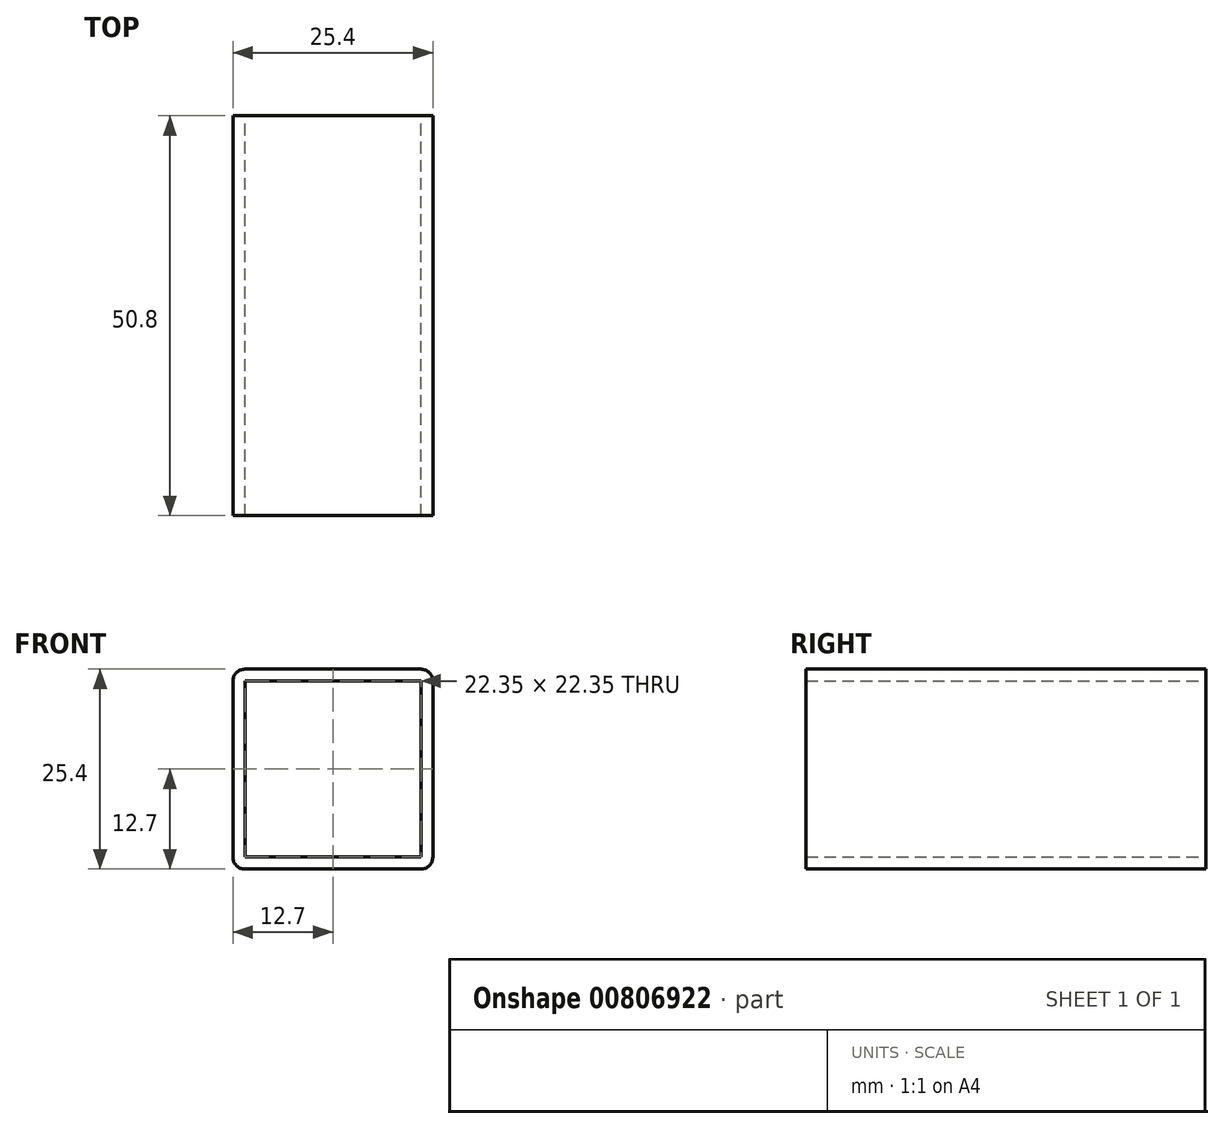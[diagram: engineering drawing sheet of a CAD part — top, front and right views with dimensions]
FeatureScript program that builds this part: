
annotation { "Feature Type Name" : "Feature", "Feature Type Description" : "" }
export const myFeature = defineFeature(function(context is Context, id is Id, definition is map)
    precondition{}
    {
        {
            var Q0;
            Q0=qCreatedBy(makeId("Front.planeOp"),FACE);
            var sketch = newSketch(context, id + "F0", { "sketchPlane" : qUnion([Q0])});
            skLineSegment(sketch, "E0.bottom", {"start": v(1.52, 0) * mm, "end": v(23.88, 0) * mm});
            skLineSegment(sketch, "E0.top", {"start": v(1.52, 25.4) * mm, "end": v(23.88, 25.4) * mm});
            skLineSegment(sketch, "E0.left", {"start": v(0, 1.52) * mm, "end": v(0, 23.88) * mm});
            skLineSegment(sketch, "E0.right", {"start": v(25.4, 1.52) * mm, "end": v(25.4, 23.88) * mm});
            skPoint(sketch, "E1.visualSharp", {"position": v(0, 25.4) * mm});
            skArc(sketch, "E1.filletArc", {"start": v(1.52, 25.4) * mm, "mid": v(0.45, 24.95) * mm, "end": v(0, 23.88) * mm});
            skPoint(sketch, "E2.visualSharp", {"position": v(25.4, 25.4) * mm});
            skArc(sketch, "E2.filletArc", {"start": v(25.4, 23.88) * mm, "mid": v(24.95, 24.95) * mm, "end": v(23.88, 25.4) * mm});
            skPoint(sketch, "E3.visualSharp", {"position": v(25.4, 0) * mm});
            skArc(sketch, "E3.filletArc", {"start": v(23.88, 0) * mm, "mid": v(24.95, 0.45) * mm, "end": v(25.4, 1.52) * mm});
            skPoint(sketch, "E4.visualSharp", {"position": v(0, 0) * mm});
            skArc(sketch, "E4.filletArc", {"start": v(0, 1.52) * mm, "mid": v(0.45, 0.45) * mm, "end": v(1.52, 0) * mm});
            skLineSegment(sketch, "E5.0", {"start": v(23.88, 1.52) * mm, "end": v(23.88, 23.88) * mm});
            skLineSegment(sketch, "E5.1", {"start": v(1.52, 1.52) * mm, "end": v(23.88, 1.52) * mm});
            skLineSegment(sketch, "E5.2", {"start": v(1.52, 1.52) * mm, "end": v(1.52, 23.88) * mm});
            skLineSegment(sketch, "E5.3", {"start": v(1.52, 23.88) * mm, "end": v(23.88, 23.88) * mm});
            skSolve(sketch);
        }
        {
            var Q0;
            Q0 = qSketchRegion(id + "F0", true);
            extrude(context, id + "F1", {"entities" : qUnion([Q0]), "depth" : 50.8 * mm, "offsetDistance" : 25.4 * mm});
        }
    });
